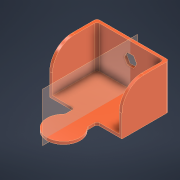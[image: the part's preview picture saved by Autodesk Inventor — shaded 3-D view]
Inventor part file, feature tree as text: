
AUTODESK INVENTOR PART (.ipt)
format: ipt  version: 2022 (Build 260153000, 153)  size: 338,944 bytes
history: native  units: in
note: dims shown in document units (in); Inventor stores cm internally (conversion verified against a paired STEP export)
features: extrude x3, fillet x3, sketch x3, plane x1, projected_geometry x1
ambient origin geometry x8: Origin, YZ Plane, XZ Plane, XY Plane, X Axis, Y Axis, Z Axis, Center Point
bodies: Body1 (feature_tree)
feature tree (11):
  extrude  "Extrusion2"  Depth=2.0in
  fillet  "Fillet2"  Radius=1.0in
  extrude  "Extrusion3"  Depth=1.0in
  fillet  "Fillet3"  Radius=1.5in
  fillet  "Fillet4"  Radius=0.125in
  plane  "Work Plane1"
  extrude  "Extrusion6"  Depth=0.125in
  sketch  "Sketch1"  dims[d0=3.0in d1=2.0in d2=1.0in]
  sketch  "Sketch2"  dims[d3=1.0in d4=1.0in d5=1.5in d9=0.125in d10=0.0in]
  sketch  "Sketch5"  dims[d11=0.125in d12=0.125in d13=0.125in d14=0.125in d15=2.0in d16=0.0in d17=0.125in d18=1.0in d27=0.5in d28=0.5in d29=1.0in d30=0.0in]
  projected_geometry  "Projected Loop1"
